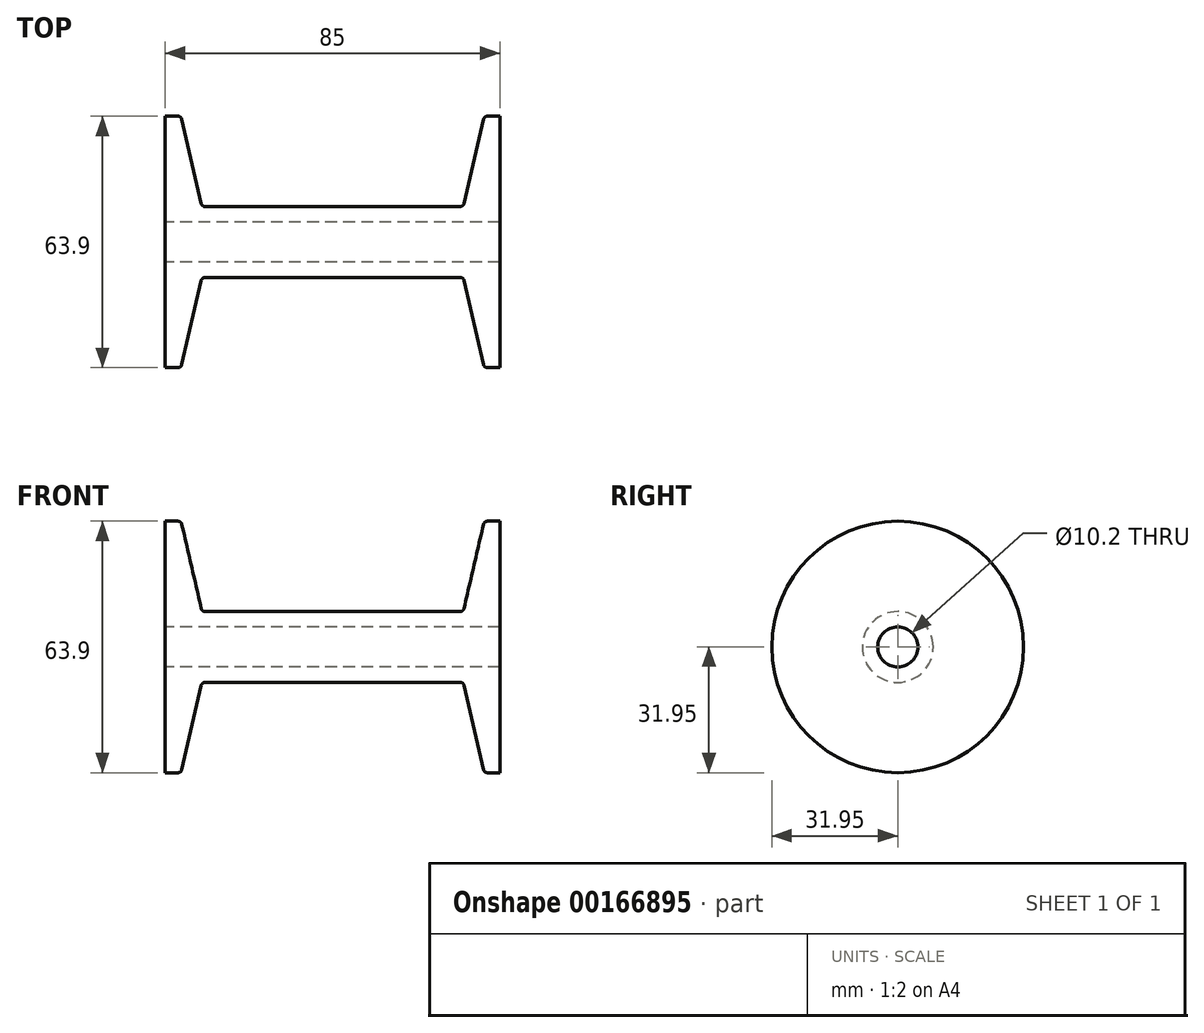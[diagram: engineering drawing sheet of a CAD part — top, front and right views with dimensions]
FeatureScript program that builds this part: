
annotation { "Feature Type Name" : "Feature", "Feature Type Description" : "" }
export const myFeature = defineFeature(function(context is Context, id is Id, definition is map)
    precondition{}
    {
        {
            var Q0;
            Q0=qCreatedBy(makeId("Front.planeOp"),FACE);
            var sketch = newSketch(context, id + "F0", { "sketchPlane" : qUnion([Q0])});
            skLineSegment(sketch, "E0", {"start": v(0, 0) * mm, "end": v(42.5, 0) * mm, "construction": true});
            skLineSegment(sketch, "E1", {"start": v(42.5, 5.1) * mm, "end": v(0, 5.1) * mm});
            skLineSegment(sketch, "E2", {"start": v(42.5, 5.1) * mm, "end": v(42.5, 31.95) * mm});
            skLineSegment(sketch, "E3", {"start": v(42.5, 31.95) * mm, "end": v(39.3, 31.95) * mm});
            skLineSegment(sketch, "E4", {"start": v(38.32, 31.17) * mm, "end": v(33.38, 9.78) * mm});
            skLineSegment(sketch, "E5", {"start": v(32.4, 9) * mm, "end": v(0, 9) * mm});
            skLineSegment(sketch, "E6", {"start": v(0, 0) * mm, "end": v(0, 29.08) * mm, "construction": true});
            skPoint(sketch, "E7.visualSharp", {"position": v(33.2, 9) * mm});
            skArc(sketch, "E7.filletArc", {"start": v(32.4, 9) * mm, "mid": v(33.03, 9.22) * mm, "end": v(33.38, 9.78) * mm});
            skPoint(sketch, "E8.visualSharp", {"position": v(38.5, 31.95) * mm});
            skArc(sketch, "E8.filletArc", {"start": v(39.3, 31.95) * mm, "mid": v(38.67, 31.73) * mm, "end": v(38.32, 31.17) * mm});
            skArc(sketch, "E9.MirrorCS", {"start": v(-39.3, 31.95) * mm, "mid": v(-38.67, 31.73) * mm, "end": v(-38.32, 31.17) * mm});
            skArc(sketch, "E10.MirrorCS", {"start": v(-32.4, 9) * mm, "mid": v(-33.03, 9.22) * mm, "end": v(-33.38, 9.78) * mm});
            skLineSegment(sketch, "E11.MirrorCS", {"start": v(-42.5, 31.95) * mm, "end": v(-39.3, 31.95) * mm});
            skPoint(sketch, "E12.MirrorP", {"position": v(-33.2, 9) * mm});
            skLineSegment(sketch, "E13.MirrorCS", {"start": v(-42.5, 5.1) * mm, "end": v(0, 5.1) * mm});
            skLineSegment(sketch, "E14.MirrorCS", {"start": v(-32.4, 9) * mm, "end": v(0, 9) * mm});
            skLineSegment(sketch, "E15.MirrorCS", {"start": v(-38.32, 31.17) * mm, "end": v(-33.38, 9.78) * mm});
            skLineSegment(sketch, "E16.MirrorCS", {"start": v(-42.5, 5.1) * mm, "end": v(-42.5, 31.95) * mm});
            skPoint(sketch, "E17.MirrorP", {"position": v(-38.5, 31.95) * mm});
            skSolve(sketch);
        }
        {
            var Q0;
            Q0=qSketchRegion(id+"F0",true);
            var Q1;
            Q1=sQuery(id+"F0.wireOp",EDGE,"E0");
            revolve(context, id + "F1", {"entities" : qUnion([Q0]), "axis" : qUnion([Q1]), "revolveType" : RevolveType.FULL});
        }
    });
